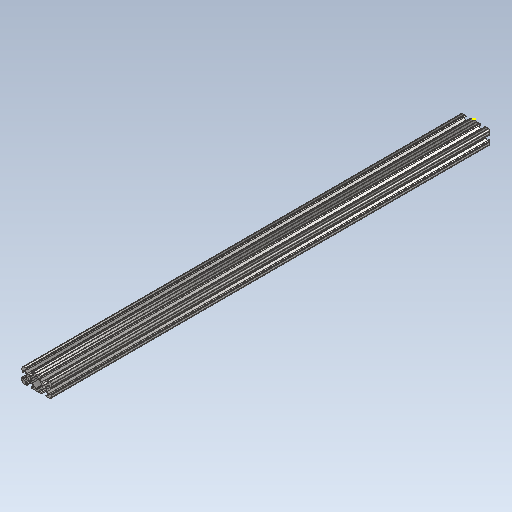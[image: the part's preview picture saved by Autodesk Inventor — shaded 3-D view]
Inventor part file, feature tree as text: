
AUTODESK INVENTOR PART (.ipt)
format: ipt  version: 2020 (Build 240168000, 168)  size: 391,680 bytes
history: native  units: in
note: dims shown in document units (in); Inventor stores cm internally (conversion verified against a paired STEP export)
features: other x3, sketch x2
ambient origin geometry x8: Origin, YZ Plane, XZ Plane, XY Plane, X Axis, Y Axis, Z Axis, Center Point
bodies: Solid1 (feature_tree)
feature tree (5):
  other  "25in 2x1 T Slot1.ipt"
  other  "Solid1::25in 2x1 T Slot1.ipt"
  other  "TaggingFeature1"
  sketch  "Sketch1"  dims[d0=0.3937in]
  sketch  "Sketch2"
